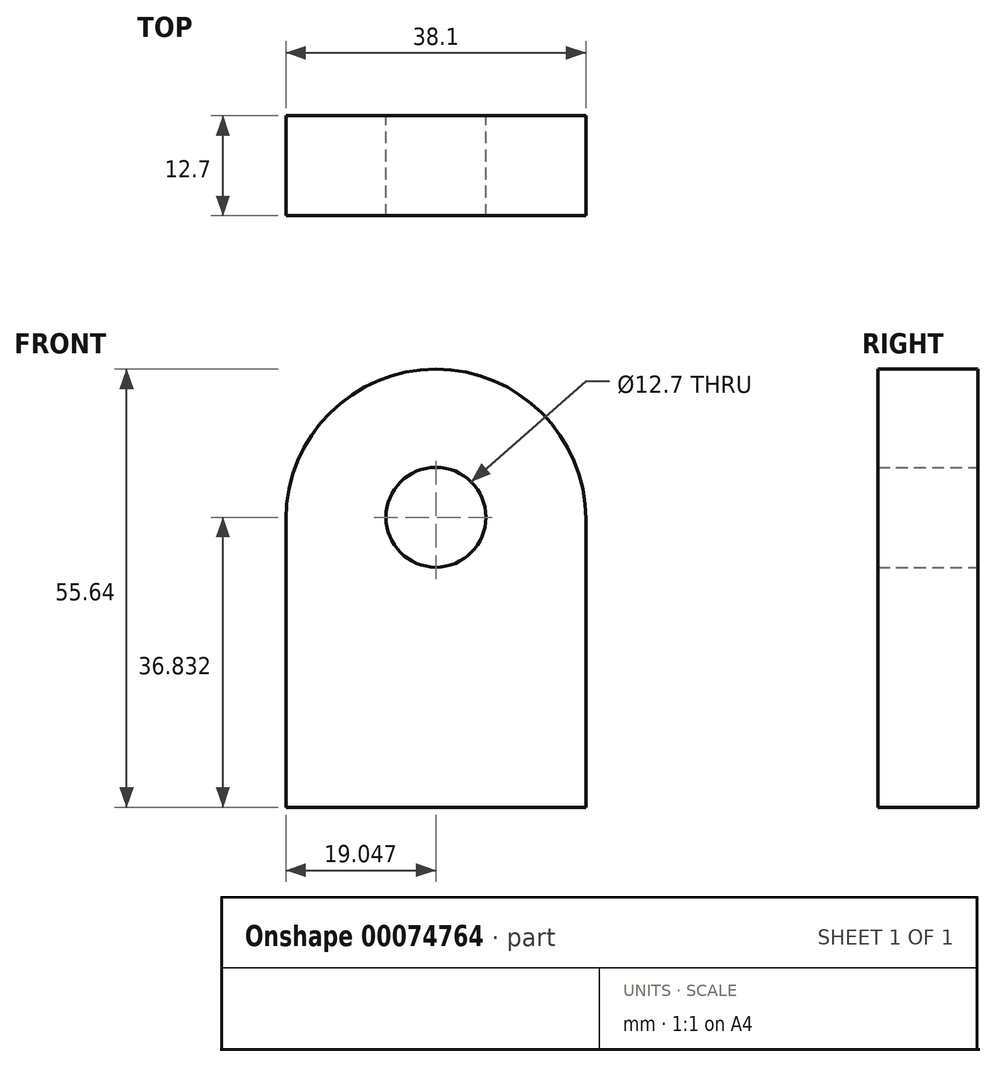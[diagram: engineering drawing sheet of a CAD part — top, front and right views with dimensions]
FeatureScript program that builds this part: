
annotation { "Feature Type Name" : "Feature", "Feature Type Description" : "" }
export const myFeature = defineFeature(function(context is Context, id is Id, definition is map)
    precondition{}
    {
        {
            var Q0;
            Q0=qCreatedBy(makeId("Front.planeOp"),FACE);
            var sketch = newSketch(context, id + "F0", { "sketchPlane" : qUnion([Q0])});
            skLineSegment(sketch, "E0", {"start": v(-58.34, 11.03) * mm, "end": v(-20.24, 11.03) * mm});
            skLineSegment(sketch, "E1", {"start": v(-20.24, 11.03) * mm, "end": v(-20.24, 47.62) * mm});
            skLineSegment(sketch, "E2", {"start": v(-58.34, 11.03) * mm, "end": v(-58.34, 47.62) * mm});
            skArc(sketch, "E3", {"start": v(-20.24, 47.62) * mm, "mid": v(-39.3, 66.67) * mm, "end": v(-58.34, 47.62) * mm});
            skSolve(sketch);
        }
        {
            var Q0;
            Q0=makeQuery(id+"F0.imprint","IMPRINT",FACE,{"disambiguationData":[TD([[makeQuery(id+"F0.imprint","IMPRINT",EDGE,{"derivedFrom":sQuery(id+"F0.wireOp",EDGE,"E0")}),1.0]])]});
            extrude(context, id + "F1", {"entities" : qUnion([Q0]), "depth" : 12.7 * mm});
        }
        {
            var Q0;
            Q0=makeQuery(id+"F1.opExtrude","CAP_FACE",FACE,{"disambiguationData":[OSD([sQuery(id+"F0.wireOp",EDGE,"E0"),sQuery(id+"F0.wireOp",EDGE,"E1"),sQuery(id+"F0.wireOp",EDGE,"E2"),sQuery(id+"F0.wireOp",EDGE,"E3")])],"isStart":false});
            var sketch = newSketch(context, id + "F2", { "sketchPlane" : qUnion([Q0])});
            skPoint(sketch, "E4", {"position": v(-39.3, 47.86) * mm});
            skSolve(sketch);
        }
        {
            var Q0;
            Q0=sQuery(id+"F2.wireOp",VERTEX,"E4");
            var Q1;
            Q1=makeQuery(id+"F1.opExtrude","SWEPT_BODY",BODY,{"disambiguationData":[OSD([sQuery(id+"F0.wireOp",EDGE,"E0"),sQuery(id+"F0.wireOp",EDGE,"E1"),sQuery(id+"F0.wireOp",EDGE,"E2"),sQuery(id+"F0.wireOp",EDGE,"E3")])]});
            hole(context, id + "F3", {"style" : HoleStyle.SIMPLE, "holeDiameter" : 12.7 * mm, "endStyle" : HoleEndStyle.THROUGH, "locations" : qUnion([Q0]), "scope" : qUnion([Q1])});
        }
    });
